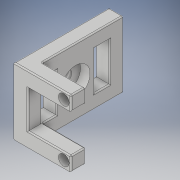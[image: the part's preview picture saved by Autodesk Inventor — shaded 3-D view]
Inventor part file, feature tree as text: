
AUTODESK INVENTOR PART (.ipt)
format: ipt  version: 2017 (Build 210142000, 142)  size: 244,736 bytes
history: native  units: in
note: dims shown in document units (in); Inventor stores cm internally (conversion verified against a paired STEP export)
features: sketch x4, extrude x4, projected_geometry x3, hole x1, fillet x1
ambient origin geometry x8: Origin, YZ Plane, XZ Plane, XY Plane, X Axis, Y Axis, Z Axis, Center Point
bodies: Solid1 (feature_tree)
feature tree (13):
  sketch  "Sketch1"  dims[d8=0.51in d9=0.1975in]
  extrude  "Extrusion1"  Depth=0.1975in
  extrude  "Extrusion2"  Depth=0.1825in
  extrude  "Extrusion3"  Depth=0.1875in
  extrude  "Extrusion5"  Depth=0.015in TaperAngle=0.0deg
  hole  "Hole1"  [1 undecoded]
  fillet  "Fillet1"  Radius=0.14in
  sketch  "Sketch2"  dims[d10=0.1775in d11=0.1825in]
  projected_geometry  "Projected Loop1"
  sketch  "Sketch3"  dims[d12=0.1875in d13=0.0in d14=0.375in]
  projected_geometry  "Projected Loop5"
  sketch  "Sketch5"  dims[d15=0.4375in d17=0.125in d18=0.0in d21=0.75in d22=0.14in d23=0.0938in d24=0.14in d25=0.1875in d26=0.0in d28=0.1825in d29=0.1775in d31=0.247in d32=0.1235in d33=0.75in d34=0.0938in d35=0.0938in d37=1.25in d38=1.25in d39=0.875in d43=0.1975in d44=0.0in d45=0.1875in d46=0.0938in d47=0.0in d48=0.51in d49=0.1825in d50=1.0in d51=0.0in d52=1.25in d53=0.625in d54=0.145in d55=0.38in d56=0.375in d57=0.25in d58=0.5635in d59=0.588in d60=0.8108in d61=0.015in]
  projected_geometry  "Projected Loop6"
note: 1 required parameter value undecoded (feature->parameter linkage not recoverable at this tier; creation-order binding heuristic only, values carry confidence <= 0.55)
